# Revit family: Geberit Sigma ugradni vodokotlić 12 cm, 6 _ 3 litara_PRO_100366
name_source: partatom
category: Plumbing Fixtures
units: mm (PartAtom-declared; Revit-internal decimal feet)

## family parameters
Always vertical = Yes
Cut with Voids When Loaded = No
OmniClass Number = 23.31.19.00
Part Type = Normal
Room Calculation Point = Yes
Round Connector Dimension = Use Diameter
Shared = No
Work Plane-Based = No

## types (1)
- 109.300.00.5 Geberit Sigma ugradni vodokotlić 12 cm, 6 / 3 litara
    B = 410 mm  [stored 1.34514 ft]
    BIM datoteka, datum izmene = 2023.07.05
    BIM datoteka, proizvođač = Geberit
    BIM datoteka, verzija = GEB MG 1.6
    Broj artikla = 109.300.00.5
    CW Connection = Yes
    D1 = 90 mm
    Default Elevation = 0 mm  [stored 0 ft]
    Description = Geberit Sigma ugradni vodokotlić 12 cm, 6 / 3 litara
    EAN code basic data = 4025416724728
    Fabrički podešena količina ispiranja = 6 i 3 l
    GEB_culture = sr-RS
    GEB_generic_description = concealed cistern for toilet
    GEB_generic_manufacturer = generic
    GEB_imperial_engineering = No
    GEB_metric_engineering = Yes
    GEB_pimversion = 23.08.11
    GEB_processing_type = T
    GEB_reference = PRO_100366
    GEB_translations = {"ATT_10673":"EAN code basic data","ATT_10773":"Protočni pritisak","ATT_10807":"Opseg podešavanje veće količine vode za ispiranje","ATT_10811":"Opseg podešavanja manje količine vode za ispiranje","ATT_10832":"Maksimalna temperatura vode","ATT_10866":"Fabrički podešena količina ispiranja","applicationPurposes":"Namene","application_range":"Oblast primene","brandName":"Robna marka","characteristics":"Svojstva","connection_description1":"Opis priključka 1","GEB_connection_diameter1":"Prečnik priključka 1","connection_description2":"Opis priključka 2","GEB_connection_diameter2":"Prečnik priključka 2","connection_type_c01":"Vrsta priključka kod priključka 01","connection_type_c02":"Vrsta priključka kod priključka 02","content_creator":"BIM datoteka, proizvođač","content_date_changed":"BIM datoteka, datum izmene","content_version":"BIM datoteka, verzija","key 1000":"Broj artikla","name":"Naziv","productBrand":"Robna marka proizvoda","scopeOfDelivery":"Obim isporuke","type":"Tip","GEB_cut_length_c01":"Maksimalno skraćenje kod priključka 01","angle":"ugao","placement finished floor":"Na gornjoj ivici gotovog poda","sanitary socket":"Spojnica za prelaz","surface height":"Visina debljine poda","warning":"Upozorenje","fixed_material":"Osnovni materijal","fixed_material_01":"Osnovni materijal 01","fixed_material_02":"Osnovni materijal 02","fixed_material_03":"Osnovni materijal 03","ATT_10931":"B","ATT_10951":"H","ATT_380239":"T"}
    GEB_use_DN = Yes
    H = 510 mm  [stored 1.67323 ft]
    HW Connection = No
    IfcDescription = Geberit Sigma ugradni vodokotlić 12 cm, 6 / 3 litara
    IfcExportAs = IfcSanitaryTerminal
    IfcExportType = CISTERN
    LOD300 = No
    LOD400 = Yes
    Maksimalna temperatura vode = 25 °C
    Manufacturer = Geberit
    Model = Sigma 12 cm
    Namene = Za ozidane zidove
Za ugradnju u predzidne konstrukcije delimične ili visine etaže
Za ugradnju u instalacione zidove u visini etaže
Za podne i konzolne WC šolje
Za jednokoličinsko, dvokoličinsko ili start/stop ispiranje
    Naziv = Geberit Sigma ugradni vodokotlić 12 cm, 6 / 3 litara
    Obim isporuke = Priključak vode R 1/2", kompatibilan sa MF adapterom, sa integrisanim ugaonim ventilom i ručnim točkićem
Građevinska zaštita za revizioni otvor
Ispirno koleno sa izolacionom oblogama
Zaštitni čep
2 čelične trake za pričvršćenje
2 ugaonika za pričvršćivanje
Materijal za pričvršćivanje
    Oblast primene = sanitary systems
    Opis priključka 1 = cold water in
    Opis priključka 2 = sanitary out
    Opseg podešavanja manje količine vode za ispiranje = 2-4 l
    Opseg podešavanje veće količine vode za ispiranje = 4 / 4.5 / 6 / 7.5 l
    Osnovni materijal = Geberit, Plastic, Opaque white
    Osnovni materijal 01 = Geberit, Laminate, Ivory, Matte
    Osnovni materijal 02 = Geberit, Steel, Paint Finish, Black
    Osnovni materijal 03 = Geberit, PE-HD, Black
    Protočni pritisak = 0.1-10 bar
    Robna marka = Geberit
    Svojstva = Ugradni vodokotlić sa aktiviranjem sa prednje strane
Ugradni vodokotlić sa izolacijom protiv kondenzacije
Kod fabričkog podešavanja moguće je automatsko naknadno ispiranje
Ispirno koleno, sakriveno
Radovi na montaži i servisu na ugradnom vodokotliću bez alata
Priključak za vodu, pozadi ili gore na sredini
Građevinska zaštita štiti otvor za servisiranje od vlage i prljavštine
Građevinska zaštita za revizioni otvor koja se može seći prema dužini
    T = 120 mm  [stored 0.393701 ft]
    Tip = Sigma 12 cm
    Vent Connection = No
    Waste Connection = Yes
    cistern_bottom = 510 mm  [stored 1.67323 ft]
    cistern_depth = 120 mm  [stored 0.393701 ft]
    cistern_top_offset = 0 mm  [stored 0 ft]
    cistern_width = 410 mm  [stored 1.34514 ft]
    connection_bend = No
    flushing_water_pipe_D = 80 mm  [stored 0.262467 ft]
    outlet_flow = 0.0 L/s

note: [stored X ft] marks values corroborated as IEEE doubles in the binary element streams (Revit-internal decimal feet)

## geometry (parser evidence)
native form markers: Blend x4, Sweep x4
no freeform markers — native parametric forms only
